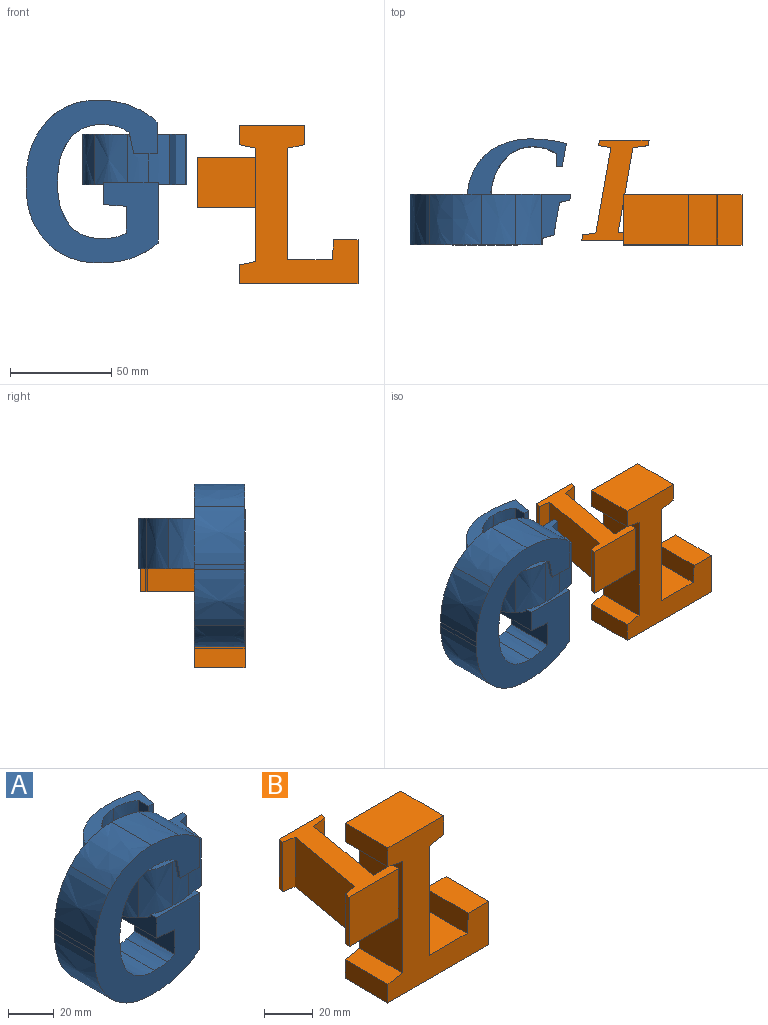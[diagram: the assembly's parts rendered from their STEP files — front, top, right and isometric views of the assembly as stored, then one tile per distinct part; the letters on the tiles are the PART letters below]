
ASSEMBLY  parts=2 mates=1
PART A: 59 faces, bbox 79.4x52.4x80.5 mm
  f0: plane 50.91x49.16mm, normal (0,0,1), area 693.8mm2, adj f2,f3,f4,f5,f15,f16,f17,f18
  f1: plane 21.44x14.14mm, normal (0,0,-1), area 169.3mm2, adj f6,f7,f8,f9,f10,f32
  f2: extruded ~25x16.28mm, area 423.5mm2, adj f0,f3,f26,f28
  f3: extruded ~25x14.75mm, area 408mm2, adj f0,f2,f4,f28
  f4: extruded ~25x16.15mm, area 421.2mm2, adj f0,f3,f5,f28,f30,f34
  f5: extruded ~23.81x10.61mm, area 170.5mm2, adj f0,f4,f6,f29,f30,f46
  f6: extruded ~25x10.43mm, area 221.4mm2, adj f1,f5,f7,f27,f29,f30,f32,f48
  f7: plane 25x16.12mm, normal (0.98,-0.17,0), area 409.3mm2, adj f1,f6,f8,f27
  f8: plane 25x5.03mm, normal (0.23,-0.97,0), area 129.2mm2, adj f1,f7,f9,f27
  f9: plane 25x2.52mm, normal (0.99,-0.17,0), area 64mm2, adj f1,f8,f10,f27
  f10: plane 25x22.12mm, normal (0,1,0), area 469.8mm2, adj f1,f9,f11,f27,f32,f33,f47,f48
  f11: plane 14.03x2.52mm, normal (-0.99,0.17,0), area 35.9mm2, adj f10,f12,f33,f47
  f12: plane 14.03x6.18mm, normal (-0.19,-0.98,0), area 88.2mm2, adj f11,f13,f33,f47
  f13: plane 14.05x14.03mm, normal (-0.98,0.18,0), area 200.2mm2, adj f12,f14,f33,f47
  f14: extruded ~21.01x8.76mm, area 130.8mm2, adj f13,f15,f33,f46,f47
  f15: extruded ~23.81x8.94mm, area 242.5mm2, adj f0,f14,f16,f33,f46
  f16: extruded ~23.81x11.43mm, area 287.6mm2, adj f0,f15,f17,f33
  f17: extruded ~25x14.44mm, area 364.5mm2, adj f0,f16,f18,f28,f33,f58
  f18: extruded ~25x9.77mm, area 310.5mm2, adj f0,f17,f19,f28
  f19: extruded ~25x10.65mm, area 284.8mm2, adj f0,f18,f20,f28
  f20: extruded ~25x11.84mm, area 313.1mm2, adj f0,f19,f21,f28
  f21: plane 25x6.44mm, normal (-1,0.01,0), area 161mm2, adj f0,f20,f22,f28
  f22: plane 25x3.1mm, normal (0,-1,0), area 77.5mm2, adj f0,f21,f23,f28
  f23: plane 25x11.4mm, normal (0.98,-0.18,0), area 289.5mm2, adj f0,f22,f24,f28
  f24: extruded ~25x17.57mm, area 444.2mm2, adj f0,f23,f25,f28
  f25: extruded ~25x16.51mm, area 427.5mm2, adj f0,f24,f26,f28
  f26: extruded ~25x11.15mm, area 393.1mm2, adj f0,f2,f25,f28
  f27: plane 21.56x14.62mm, normal (0,0,1), area 179.7mm2, adj f6,f7,f8,f9,f10,f48
  f28: plane 49.16x48.68mm, normal (0,0,-1), area 594.2mm2, adj f2,f3,f4,f17,f18,f19,f20,f21
  f29: plane 11.67x3.12mm, normal (0,0,-1), area 24.8mm2, adj f5,f6,f46,f48,f57
  f30: plane 27.23x4.06mm, normal (0,0,1), area 56.3mm2, adj f4,f5,f6,f32,f34,f57
  f31: extruded ~25x11.12mm, area 327.7mm2, adj f32,f56,f57,f58
  f32: plane 30.03x25mm, normal (1,0,0), area 725.4mm2, adj f1,f6,f10,f30,f31,f33,f57,f58
  f33: plane 25.65x19.74mm, normal (0,0,1), area 383mm2, adj f10,f11,f12,f13,f14,f15,f16,f17
  f34: plane 25x11mm, normal (-1,0,0), area 249.9mm2, adj f4,f28,f30,f35,f57,f58
  f35: plane 25x11.17mm, normal (-0.08,0,-1), area 280.2mm2, adj f34,f36,f57,f58
  f36: plane 25x13.27mm, normal (-1,0,0), area 331.8mm2, adj f35,f37,f57,f58
  f37: extruded ~25x4.59mm, area 124.6mm2, adj f36,f38,f57,f58
  f38: extruded ~25x7.65mm, area 192.9mm2, adj f37,f39,f57,f58
  f39: extruded ~25x16.12mm, area 457.4mm2, adj f38,f40,f57,f58
  f40: extruded ~25x19.04mm, area 505.4mm2, adj f39,f41,f57,f58
  f41: plane 25x2.8mm, normal (1,0,0), area 70.1mm2, adj f40,f42,f57,f58
  f42: extruded ~25x19.82mm, area 524.8mm2, adj f41,f43,f57,f58
  f43: extruded ~25x15.96mm, area 459.4mm2, adj f42,f44,f57,f58
  f44: extruded ~25x8.08mm, area 204.7mm2, adj f43,f45,f57,f58
  f45: extruded ~25x5.67mm, area 160.7mm2, adj f44,f46,f57,f58
  f46: plane 25.01x10.48mm, normal (-0.98,0,-0.21), area 229.5mm2, adj f0,f5,f14,f15,f29,f45,f47,f57
  f47: plane 19.72x11.72mm, normal (0,0,-1), area 149.3mm2, adj f10,f11,f12,f13,f14,f46,f48,f58
  f48: plane 25x15.73mm, normal (1,0,0), area 182.6mm2, adj f6,f10,f27,f29,f47,f49,f57,f58
  f49: extruded ~25x12.65mm, area 376mm2, adj f48,f50,f57,f58
  f50: extruded ~25x16.8mm, area 428.7mm2, adj f49,f51,f57,f58
  f51: extruded ~25.59x25mm, area 719.2mm2, adj f50,f52,f57,f58
  f52: extruded ~28.57x25mm, area 772.8mm2, adj f51,f53,f57,f58
  f53: plane 25x2.7mm, normal (-1,0,0), area 67.5mm2, adj f52,f54,f57,f58
  f54: extruded ~27.58x25mm, area 751.4mm2, adj f53,f55,f57,f58
  f55: extruded ~25.79x25mm, area 718.3mm2, adj f54,f56,f57,f58
  f56: extruded ~25x18.48mm, area 471.2mm2, adj f31,f55,f57,f58
  f57: plane 80.49x65.32mm, normal (0,-1,0), area 2725.5mm2, adj f29,f30,f31,f32,f34,f35,f36,f37
  f58: plane 80.49x65.32mm, normal (0,1,0), area 2723.8mm2, adj f17,f28,f31,f32,f33,f34,f35,f36
PART B: 30 faces, bbox 79.2x51.8x78.2 mm
  f0: plane 25x9.4mm, normal (-1,0,0), area 235.1mm2, adj f1,f13,f14,f15
  f1: plane 58.83x25mm, normal (0,0,-1), area 1470.6mm2, adj f0,f2,f14,f15
  f2: plane 25x21.87mm, normal (1,0,0), area 546.7mm2, adj f1,f3,f14,f15
  f3: plane 25x11.98mm, normal (0,0,1), area 299.5mm2, adj f2,f4,f14,f15
  f4: plane 25x9.83mm, normal (-1,0,0.08), area 246.5mm2, adj f3,f5,f14,f15
  f5: plane 25x22.07mm, normal (0,0,1), area 551.8mm2, adj f4,f6,f14,f15
  f6: plane 55.11x25mm, normal (1,0,0), area 1377.8mm2, adj f5,f7,f14,f15
  f7: plane 25x8.37mm, normal (0.19,0,-0.98), area 213.2mm2, adj f6,f8,f14,f15
  f8: plane 25x9.45mm, normal (1,0,0), area 236.4mm2, adj f7,f9,f14,f15
  f9: plane 32.39x25mm, normal (0,0,1), area 809.7mm2, adj f8,f10,f14,f15
  f10: plane 25x9.45mm, normal (-1,0,0), area 236.4mm2, adj f9,f11,f14,f15
  f11: plane 25x8.32mm, normal (-0.19,0,-0.98), area 211.9mm2, adj f10,f12,f14,f15
  f12: plane 56.13x25mm, normal (-1,0,0), area 1300.9mm2, adj f11,f13,f14,f15,f26,f27,f28,f29
  f13: plane 25x8.32mm, normal (-0.19,0,0.98), area 211.9mm2, adj f0,f12,f14,f15
  f14: plane 78.22x58.83mm, normal (0,-1,0), area 2024.3mm2, adj f0,f1,f2,f3,f4,f5,f6,f7
  f15: plane 78.22x58.83mm, normal (0,1,0), area 2024.3mm2, adj f0,f1,f2,f3,f4,f5,f6,f7
  f16: plane 25x4.18mm, normal (0,1,0), area 104.5mm2, adj f17,f27,f28,f29
  f17: plane 42.02x25mm, normal (0.98,-0.17,0), area 1066.6mm2, adj f16,f18,f28,f29
  f18: plane 25x7.47mm, normal (0.13,-0.99,0), area 188.3mm2, adj f17,f19,f28,f29
  f19: plane 25x2.7mm, normal (0.98,-0.18,0), area 68.5mm2, adj f18,f20,f28,f29
  f20: plane 25x24.53mm, normal (0,1,0), area 613.1mm2, adj f19,f21,f28,f29
  f21: plane 25x2.7mm, normal (-0.98,0.18,0), area 68.5mm2, adj f20,f22,f28,f29
  f22: plane 25x6.14mm, normal (-0.16,-0.99,0), area 155.5mm2, adj f21,f23,f28,f29
  f23: plane 42.23x25mm, normal (-0.98,0.17,0), area 1072mm2, adj f22,f24,f28,f29
  f24: plane 25x6.55mm, normal (-0.15,0.99,0), area 165.6mm2, adj f23,f25,f28,f29
  f25: plane 25x2.7mm, normal (-0.99,0.16,0), area 68.4mm2, adj f24,f26,f28,f29
  f26: plane 28.73x25mm, normal (0,-1,0), area 718.1mm2, adj f12,f25,f28,f29
  f27: extruded ~25x6.6mm, area 165.1mm2, adj f12,f16,f28,f29
  f28: plane 49.61x33.3mm, normal (0,0,1), area 649mm2, adj f12,f16,f17,f18,f19,f20,f21,f22
  f29: plane 49.61x33.3mm, normal (0,0,-1), area 649mm2, adj f12,f16,f17,f18,f19,f20,f21,f22
PLACE A t=(-36.6,-52.14,12.19)mm
PLACE B t=(-31.41,-52.19,0.69)mm
MATE parallel B.f0 <-> A.f32  axis (-1,0,0) through (-12.54,-64.69,-32.15)mm
